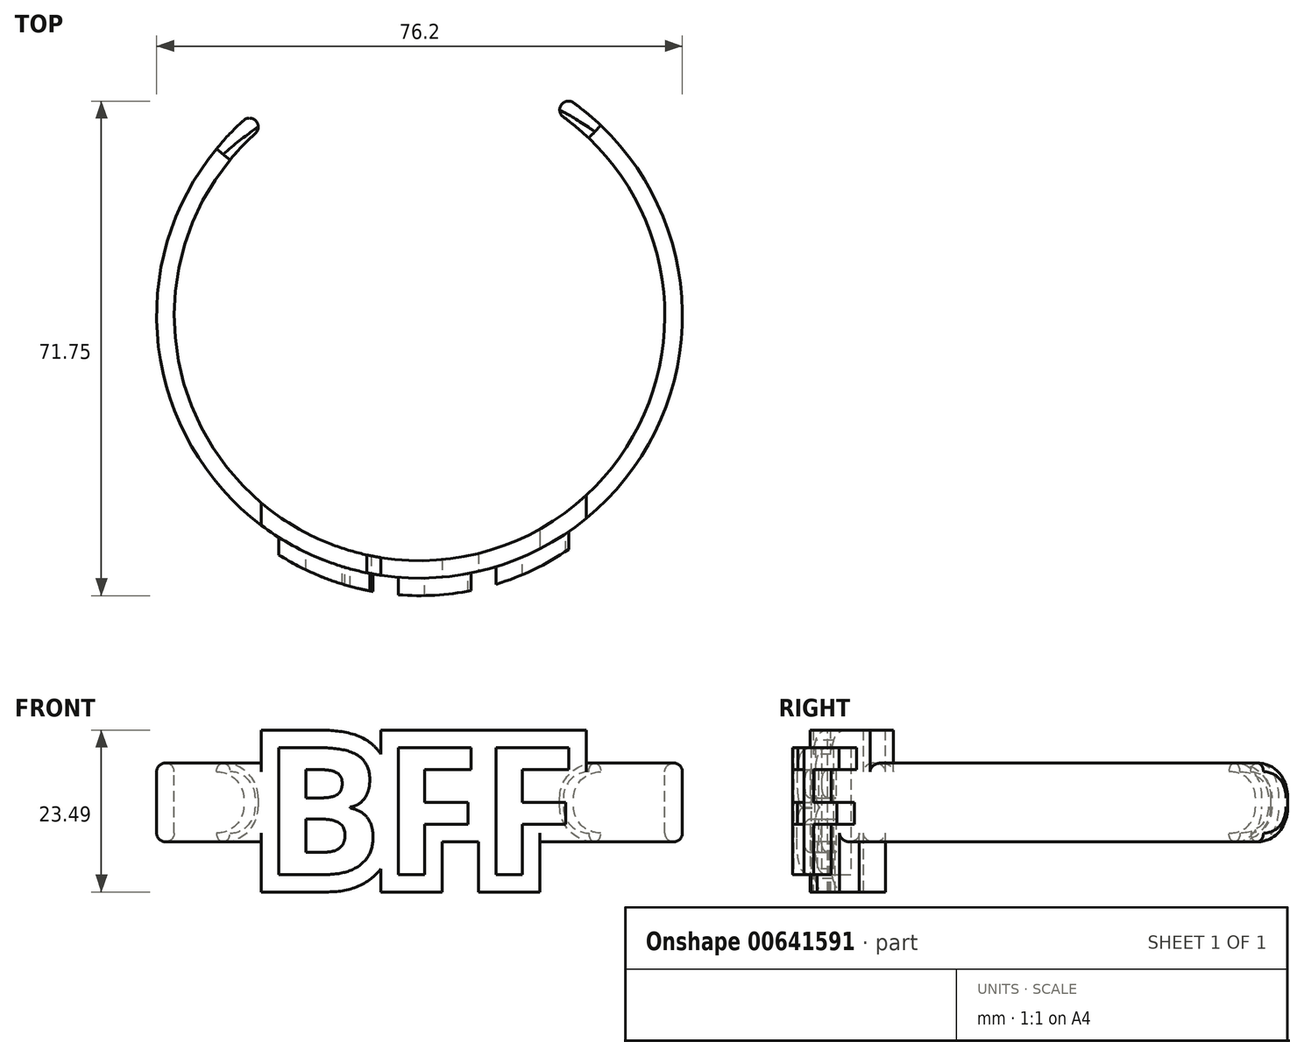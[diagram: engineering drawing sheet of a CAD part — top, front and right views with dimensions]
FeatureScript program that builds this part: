
annotation { "Feature Type Name" : "Feature", "Feature Type Description" : "" }
export const myFeature = defineFeature(function(context is Context, id is Id, definition is map)
    precondition{}
    {
        {
            var Q0;
            Q0=qCreatedBy(makeId("Top.planeOp"),FACE);
            var sketch = newSketch(context, id + "F0", { "sketchPlane" : qUnion([Q0])});
            skCircle(sketch, "E0", {"center": v(0, 0) * mm, "radius": 38.1 * mm});
            skSolve(sketch);
        }
        {
            var Q0;
            Q0 = qSketchRegion(id + "F0", true);
            extrude(context, id + "F1", {"entities" : qUnion([Q0]), "depth" : 25.4 * mm, "offsetDistance" : 25.4 * mm});
        }
        {
            var Q0;
            Q0=qCreatedBy(makeId("Front.planeOp"),FACE);
            var sketch = newSketch(context, id + "F2", { "sketchPlane" : qUnion([Q0])});
            skText(sketch, "E1", { "text": "BFF", "fontName": "OpenSans-Bold.ttf"});
            const initialGuessF2  = {"E1": [-0.0227, 0.00313, 1, 0, 0.01856]};
            skSetInitialGuess(sketch, initialGuessF2);
            skSolve(sketch);
        }
        {
            var Q0;
            Q0 = qSketchRegion(id + "F2", true);
            var Q1;
            Q1=makeQuery(id+"F1.opExtrude","SWEPT_FACE",FACE,{"disambiguationData":[OSD([sQuery(id+"F0.wireOp",EDGE,"E0")])]});
            extrude(context, id + "F3", {"entities" : qUnion([Q0]), "operationType" : NewBodyOperationType.ADD, "endBound" : BoundingType.UP_TO_SURFACE, "depth" : 25.4 * mm, "endBoundEntityFace" : qUnion([Q1]), "hasOffset" : true, "offsetDistance" : 2.54 * mm, "offsetOppositeDirection" : true});
        }
        {
            var Q0;
            Q0=qCreatedBy(makeId("Front.planeOp"),FACE);
            var sketch = newSketch(context, id + "F4", { "sketchPlane" : qUnion([Q0])});
            skLineSegment(sketch, "E2.0", {"start": v(-14.66, 24.08) * mm, "end": v(-22.92, 24.08) * mm});
            skFitSpline(sketch, "E2.1", {"points": [v(-7.62, 22.57) * mm, v(-7.79, 22.68) * mm, v(-8.13, 22.87) * mm, v(-8.63, 23.1) * mm, v(-9.11, 23.3) * mm, v(-9.75, 23.5) * mm, v(-10.52, 23.7) * mm, v(-11.4, 23.86) * mm, v(-12.24, 23.97) * mm, v(-13.34, 24.06) * mm, v(-14.14, 24.08) * mm, v(-14.66, 24.08) * mm]});
            skLineSegment(sketch, "E2.2", {"start": v(-22.92, 24.08) * mm, "end": v(-22.92, 19.3) * mm});
            skFitSpline(sketch, "E2.3", {"points": [v(-4.66, 16.88) * mm, v(-4.66, 17.12) * mm, v(-4.68, 17.61) * mm, v(-4.77, 18.25) * mm, v(-4.88, 18.77) * mm, v(-5.03, 19.3) * mm, v(-5.29, 19.98) * mm, v(-5.65, 20.64) * mm, v(-6, 21.13) * mm, v(-6.3, 21.47) * mm, v(-6.6, 21.8) * mm, v(-7.04, 22.18) * mm, v(-7.39, 22.42) * mm, v(-7.62, 22.57) * mm]});
            skLineSegment(sketch, "E2.5", {"start": v(-22.92, 0.6) * mm, "end": v(-13.5, 0.6) * mm});
            skFitSpline(sketch, "E2.6", {"points": [v(-13.5, 0.6) * mm, v(-13, 0.6) * mm, v(-12.22, 0.63) * mm, v(-11.14, 0.77) * mm, v(-10.3, 0.95) * mm, v(-9.46, 1.2) * mm, v(-8.62, 1.54) * mm, v(-7.8, 1.97) * mm, v(-7.26, 2.33) * mm, v(-7, 2.53) * mm]});
            skFitSpline(sketch, "E2.7", {"points": [v(-7, 2.53) * mm, v(-6.78, 2.7) * mm, v(-6.36, 3.07) * mm, v(-5.77, 3.71) * mm, v(-5.25, 4.44) * mm, v(-4.84, 5.22) * mm, v(-4.53, 6.05) * mm, v(-4.33, 6.87) * mm, v(-4.22, 7.68) * mm, v(-4.2, 8.21) * mm, v(-4.2, 8.47) * mm]});
            skLineSegment(sketch, "E3.0", {"start": v(-5.6, 0.6) * mm, "end": v(3.32, 0.6) * mm});
            skLineSegment(sketch, "E3.1", {"start": v(-5.6, 24.08) * mm, "end": v(-5.6, 20.53) * mm});
            skLineSegment(sketch, "E3.2", {"start": v(3.32, 0.6) * mm, "end": v(3.32, 7.87) * mm});
            skLineSegment(sketch, "E3.4", {"start": v(3.32, 7.87) * mm, "end": v(8.55, 7.87) * mm});
            skLineSegment(sketch, "E4.0", {"start": v(8.55, 0.6) * mm, "end": v(17.47, 0.6) * mm});
            skLineSegment(sketch, "E4.1", {"start": v(8.55, 7.87) * mm, "end": v(8.55, 0.6) * mm});
            skLineSegment(sketch, "E4.2", {"start": v(17.47, 0.6) * mm, "end": v(17.47, 7.87) * mm});
            skLineSegment(sketch, "E4.4", {"start": v(17.47, 7.87) * mm, "end": v(23.7, 7.87) * mm});
            skLineSegment(sketch, "E4.7", {"start": v(24.18, 19.3) * mm, "end": v(24.18, 24.08) * mm});
            skLineSegment(sketch, "E5.trimOffspring", {"start": v(-5.6, 3.95) * mm, "end": v(-5.6, 0.6) * mm});
            skLineSegment(sketch, "E6", {"start": v(-5.6, 24.08) * mm, "end": v(24.18, 24.08) * mm});
            skLineSegment(sketch, "E7.bottom", {"start": v(-48.1, 19.3) * mm, "end": v(-22.92, 19.3) * mm});
            skLineSegment(sketch, "E7.top", {"start": v(-48.1, 7.87) * mm, "end": v(-22.92, 7.87) * mm});
            skLineSegment(sketch, "E8.bottom", {"start": v(24.18, 19.3) * mm, "end": v(51.49, 19.3) * mm});
            skLineSegment(sketch, "E8.top", {"start": v(23.7, 7.87) * mm, "end": v(51.49, 7.87) * mm});
            skLineSegment(sketch, "E8.left", {"start": v(23.7, 7.87) * mm, "end": v(23.7, 7.87) * mm});
            skLineSegment(sketch, "E9.trimOffspring", {"start": v(-22.92, 7.87) * mm, "end": v(-22.92, 0.6) * mm});
            skLineSegment(sketch, "E10", {"start": v(-48.1, 19.3) * mm, "end": v(-48.1, 27.27) * mm});
            skLineSegment(sketch, "E11", {"start": v(-48.1, 27.27) * mm, "end": v(51.82, 27.27) * mm});
            skLineSegment(sketch, "E12", {"start": v(51.82, 27.27) * mm, "end": v(51.49, 19.3) * mm});
            skLineSegment(sketch, "E13", {"start": v(51.49, 7.87) * mm, "end": v(51.49, -5.58) * mm});
            skLineSegment(sketch, "E14", {"start": v(51.49, -5.58) * mm, "end": v(-48.1, -5.58) * mm});
            skLineSegment(sketch, "E15", {"start": v(-48.1, -5.58) * mm, "end": v(-48.1, 7.87) * mm});
            skSolve(sketch);
        }
        {
            var Q0;
            Q0 = qSketchRegion(id + "F4", true);
            extrude(context, id + "F5", {"entities" : qUnion([Q0]), "operationType" : NewBodyOperationType.REMOVE, "endBound" : BoundingType.SYMMETRIC, "oppositeDirection" : true, "depth" : 127 * mm, "offsetDistance" : 25.4 * mm});
        }
        {
            var Q0;
            Q0=qCreatedBy(makeId("Top.planeOp"),FACE);
            var sketch = newSketch(context, id + "F6", { "sketchPlane" : qUnion([Q0])});
            skCircle(sketch, "E16", {"center": v(0, 0) * mm, "radius": 35.56 * mm});
            skSolve(sketch);
        }
        {
            var Q0;
            Q0 = qSketchRegion(id + "F6", true);
            extrude(context, id + "F7", {"entities" : qUnion([Q0]), "operationType" : NewBodyOperationType.REMOVE, "endBound" : BoundingType.SYMMETRIC, "oppositeDirection" : true, "depth" : 127 * mm, "offsetDistance" : 25.4 * mm});
        }
        {
            var Q0;
            Q0=makeQuery(id+"F5.boolean.opBoolean","COPY",FACE,{"derivedFrom":makeQuery(id+"F5.opExtrude","SWEPT_FACE",FACE,{"disambiguationData":[OSD([sQuery(id+"F4.wireOp",EDGE,"E8.bottom")])]})});
            var sketch = newSketch(context, id + "F8", { "sketchPlane" : qUnion([Q0])});
            skLineSegment(sketch, "E17.bottom", {"start": v(-38.63, 46.04) * mm, "end": v(42.06, 46.04) * mm});
            skLineSegment(sketch, "E17.top", {"start": v(-38.63, 18.38) * mm, "end": v(42.06, 18.38) * mm});
            skLineSegment(sketch, "E17.left", {"start": v(-38.63, 46.04) * mm, "end": v(-38.63, 18.38) * mm});
            skLineSegment(sketch, "E17.right", {"start": v(42.06, 46.04) * mm, "end": v(42.06, 18.38) * mm});
            skSolve(sketch);
        }
        {
            var Q0;
            Q0 = qSketchRegion(id + "F8", true);
            extrude(context, id + "F9", {"entities" : qUnion([Q0]), "operationType" : NewBodyOperationType.REMOVE, "depth" : 25.4 * mm, "offsetDistance" : 25.4 * mm});
        }
        {
            var Q0;
            Q0=makeQuery(id+"F5.boolean.opBoolean","COPY",FACE,{"derivedFrom":makeQuery(id+"F5.opExtrude","SWEPT_FACE",FACE,{"disambiguationData":[OSD([sQuery(id+"F4.wireOp",EDGE,"E7.top")])]})});
            var sketch = newSketch(context, id + "F10", { "sketchPlane" : qUnion([Q0])});
            skLineSegment(sketch, "E18.bottom", {"start": v(-23.37, -22.44) * mm, "end": v(20.32, -22.44) * mm});
            skLineSegment(sketch, "E18.top", {"start": v(-23.37, -47.04) * mm, "end": v(20.32, -47.04) * mm});
            skLineSegment(sketch, "E18.left", {"start": v(-23.37, -22.44) * mm, "end": v(-23.37, -47.04) * mm});
            skLineSegment(sketch, "E18.right", {"start": v(20.32, -22.44) * mm, "end": v(20.32, -47.04) * mm});
            skSolve(sketch);
        }
        {
            var Q0;
            Q0 = qSketchRegion(id + "F10", true);
            extrude(context, id + "F11", {"entities" : qUnion([Q0]), "operationType" : NewBodyOperationType.REMOVE, "endBound" : BoundingType.SYMMETRIC, "depth" : 50.8 * mm, "offsetDistance" : 25.4 * mm});
        }
        {
            var Q0;
            Q0=makeQuery(id+"F11.boolean.opBoolean","INTERSECT",EDGE,{"derivedFrom":[makeQuery(id+"F5.boolean.opBoolean","COPY",FACE,{"derivedFrom":makeQuery(id+"F5.opExtrude","SWEPT_FACE",FACE,{"disambiguationData":[OSD([sQuery(id+"F4.wireOp",EDGE,"E7.top")])]})}),makeQuery(id+"F11.opExtrude","SWEPT_FACE",FACE,{"disambiguationData":[OSD([sQuery(id+"F10.wireOp",EDGE,"E18.left")])]})]});
            var Q1;
            Q1=makeQuery(id+"F11.boolean.opBoolean","INTERSECT",EDGE,{"derivedFrom":[makeQuery(id+"F9.boolean.opBoolean","MERGE",FACE,{"derivedFrom":[makeQuery(id+"F5.boolean.opBoolean","COPY",FACE,{"derivedFrom":makeQuery(id+"F5.opExtrude","SWEPT_FACE",FACE,{"disambiguationData":[OSD([sQuery(id+"F4.wireOp",EDGE,"E7.bottom")])]})}),makeQuery(id+"F5.boolean.opBoolean","COPY",FACE,{"derivedFrom":makeQuery(id+"F5.opExtrude","SWEPT_FACE",FACE,{"disambiguationData":[OSD([sQuery(id+"F4.wireOp",EDGE,"E8.bottom")])]})}),makeQuery(id+"F9.opExtrude","CAP_FACE",FACE,{"disambiguationData":[OSD([sQuery(id+"F8.wireOp",EDGE,"E17.bottom"),sQuery(id+"F8.wireOp",EDGE,"E17.top"),sQuery(id+"F8.wireOp",EDGE,"E17.left"),sQuery(id+"F8.wireOp",EDGE,"E17.right")])],"isStart":true})]}),makeQuery(id+"F11.opExtrude","SWEPT_FACE",FACE,{"disambiguationData":[OSD([sQuery(id+"F10.wireOp",EDGE,"E18.left")])]})]});
            var Q2;
            Q2=makeQuery(id+"F11.boolean.opBoolean","INTERSECT",EDGE,{"derivedFrom":[makeQuery(id+"F5.boolean.opBoolean","COPY",FACE,{"derivedFrom":makeQuery(id+"F5.opExtrude","SWEPT_FACE",FACE,{"disambiguationData":[OSD([sQuery(id+"F4.wireOp",EDGE,"E4.4"),sQuery(id+"F4.wireOp",EDGE,"E8.top")])]})}),makeQuery(id+"F11.opExtrude","SWEPT_FACE",FACE,{"disambiguationData":[OSD([sQuery(id+"F10.wireOp",EDGE,"E18.right")])]})]});
            var Q3;
            Q3=makeQuery(id+"F11.boolean.opBoolean","INTERSECT",EDGE,{"derivedFrom":[makeQuery(id+"F9.boolean.opBoolean","MERGE",FACE,{"derivedFrom":[makeQuery(id+"F5.boolean.opBoolean","COPY",FACE,{"derivedFrom":makeQuery(id+"F5.opExtrude","SWEPT_FACE",FACE,{"disambiguationData":[OSD([sQuery(id+"F4.wireOp",EDGE,"E7.bottom")])]})}),makeQuery(id+"F5.boolean.opBoolean","COPY",FACE,{"derivedFrom":makeQuery(id+"F5.opExtrude","SWEPT_FACE",FACE,{"disambiguationData":[OSD([sQuery(id+"F4.wireOp",EDGE,"E8.bottom")])]})}),makeQuery(id+"F9.opExtrude","CAP_FACE",FACE,{"disambiguationData":[OSD([sQuery(id+"F8.wireOp",EDGE,"E17.bottom"),sQuery(id+"F8.wireOp",EDGE,"E17.top"),sQuery(id+"F8.wireOp",EDGE,"E17.left"),sQuery(id+"F8.wireOp",EDGE,"E17.right")])],"isStart":true})]}),makeQuery(id+"F11.opExtrude","SWEPT_FACE",FACE,{"disambiguationData":[OSD([sQuery(id+"F10.wireOp",EDGE,"E18.right")])]})]});
            fillet(context, id + "F12", {"entities" : qUnion([Q0, Q1, Q2, Q3]), "radius" : 5.08 * mm, "tangentPropagation" : true, "allowEdgeOverflow" : false});
        }
        {
            var Q0;
            Q0=makeQuery(id+"F12.opFillet","BLEND_EDGE",EDGE,{"blendedFrom":[makeQuery(id+"F11.boolean.opBoolean","INTERSECT",EDGE,{"derivedFrom":[makeQuery(id+"F9.boolean.opBoolean","MERGE",FACE,{"derivedFrom":[makeQuery(id+"F5.boolean.opBoolean","COPY",FACE,{"derivedFrom":makeQuery(id+"F5.opExtrude","SWEPT_FACE",FACE,{"disambiguationData":[OSD([sQuery(id+"F4.wireOp",EDGE,"E7.bottom")])]})}),makeQuery(id+"F5.boolean.opBoolean","COPY",FACE,{"derivedFrom":makeQuery(id+"F5.opExtrude","SWEPT_FACE",FACE,{"disambiguationData":[OSD([sQuery(id+"F4.wireOp",EDGE,"E8.bottom")])]})}),makeQuery(id+"F9.opExtrude","CAP_FACE",FACE,{"disambiguationData":[OSD([sQuery(id+"F8.wireOp",EDGE,"E17.bottom"),sQuery(id+"F8.wireOp",EDGE,"E17.top"),sQuery(id+"F8.wireOp",EDGE,"E17.left"),sQuery(id+"F8.wireOp",EDGE,"E17.right")])],"isStart":true})]}),makeQuery(id+"F11.opExtrude","SWEPT_FACE",FACE,{"disambiguationData":[OSD([sQuery(id+"F10.wireOp",EDGE,"E18.right")])]})]}),makeQuery(id+"F7.boolean.opBoolean","COPY",FACE,{"derivedFrom":makeQuery(id+"F7.opExtrude","SWEPT_FACE",FACE,{"disambiguationData":[OSD([sQuery(id+"F6.wireOp",EDGE,"E16")])]})})],"blendedInto":[makeQuery(id+"F7.boolean.opBoolean","COPY",FACE,{"derivedFrom":makeQuery(id+"F7.opExtrude","SWEPT_FACE",FACE,{"disambiguationData":[OSD([sQuery(id+"F6.wireOp",EDGE,"E16")])]})})]});
            var Q1;
            {var subQ0=sQuery(id+"F0.wireOp",EDGE,"E0");Q1=makeQuery(id+"F12.opFillet","BLEND_EDGE",EDGE,{"blendedFrom":[makeQuery(id+"F11.boolean.opBoolean","INTERSECT",EDGE,{"derivedFrom":[makeQuery(id+"F9.boolean.opBoolean","MERGE",FACE,{"derivedFrom":[makeQuery(id+"F5.boolean.opBoolean","COPY",FACE,{"derivedFrom":makeQuery(id+"F5.opExtrude","SWEPT_FACE",FACE,{"disambiguationData":[OSD([sQuery(id+"F4.wireOp",EDGE,"E7.bottom")])]})}),makeQuery(id+"F5.boolean.opBoolean","COPY",FACE,{"derivedFrom":makeQuery(id+"F5.opExtrude","SWEPT_FACE",FACE,{"disambiguationData":[OSD([sQuery(id+"F4.wireOp",EDGE,"E8.bottom")])]})})],"fromTools":[makeQuery(id+"F9.opExtrude","CAP_FACE",FACE,{"disambiguationData":[OSD([sQuery(id+"F8.wireOp",EDGE,"E17.bottom"),sQuery(id+"F8.wireOp",EDGE,"E17.top"),sQuery(id+"F8.wireOp",EDGE,"E17.left"),sQuery(id+"F8.wireOp",EDGE,"E17.right")])],"isStart":true})]}),makeQuery(id+"F11.opExtrude","SWEPT_FACE",FACE,{"disambiguationData":[OSD([sQuery(id+"F10.wireOp",EDGE,"E18.right")])]})]}),makeQuery(id+"F3.boolean.opBoolean","SPLIT",FACE,{"disambiguationData":[TD([makeQuery(id+"F1.opExtrude","CAP_FACE",FACE,{"disambiguationData":[OSD([subQ0])],"isStart":true})])],"derivedFrom":makeQuery(id+"F1.opExtrude","SWEPT_FACE",FACE,{"disambiguationData":[OSD([subQ0])]})})],"blendedInto":[makeQuery(id+"F3.boolean.opBoolean","SPLIT",FACE,{"disambiguationData":[TD([makeQuery(id+"F1.opExtrude","CAP_FACE",FACE,{"disambiguationData":[OSD([subQ0])],"isStart":true})])],"derivedFrom":makeQuery(id+"F1.opExtrude","SWEPT_FACE",FACE,{"disambiguationData":[OSD([subQ0])]})})]});}
            var Q2;
            {var subQ0=makeQuery(id+"F5.opExtrude","SWEPT_FACE",FACE,{"disambiguationData":[OSD([sQuery(id+"F4.wireOp",EDGE,"E8.bottom")])]});var subQ1=makeQuery(id+"F5.opExtrude","SWEPT_FACE",FACE,{"disambiguationData":[OSD([sQuery(id+"F4.wireOp",EDGE,"E7.bottom")])]});var subQ2=sQuery(id+"F0.wireOp",EDGE,"E0");var subQ3=makeQuery(id+"F1.opExtrude","SWEPT_FACE",FACE,{"disambiguationData":[OSD([subQ2])]});var subQ4=makeQuery(id+"F3.boolean.opBoolean","SPLIT",FACE,{"disambiguationData":[TD([makeQuery(id+"F1.opExtrude","CAP_FACE",FACE,{"disambiguationData":[OSD([subQ2])],"isStart":true})])],"derivedFrom":subQ3});Q2=makeQuery(id+"F11.boolean.opBoolean","SPLIT",EDGE,{"disambiguationData":[TD([makeQuery(id+"F5.boolean.opBoolean","COPY",FACE,{"derivedFrom":makeQuery(id+"F5.opExtrude","SWEPT_FACE",FACE,{"disambiguationData":[OSD([sQuery(id+"F4.wireOp",EDGE,"E2.2")])]})})])],"derivedFrom":makeQuery(id+"F9.boolean.opBoolean","MERGE",EDGE,{"derivedFrom":[makeQuery(id+"F5.boolean.opBoolean","INTERSECT",EDGE,{"derivedFrom":[subQ4,subQ1]}),makeQuery(id+"F5.boolean.opBoolean","INTERSECT",EDGE,{"derivedFrom":[subQ4,subQ0]})]})});}
            var Q3;
            {var subQ0=makeQuery(id+"F7.opExtrude","SWEPT_FACE",FACE,{"disambiguationData":[OSD([sQuery(id+"F6.wireOp",EDGE,"E16")])]});var subQ1=makeQuery(id+"F5.boolean.opBoolean","COPY",FACE,{"derivedFrom":makeQuery(id+"F5.opExtrude","SWEPT_FACE",FACE,{"disambiguationData":[OSD([sQuery(id+"F4.wireOp",EDGE,"E8.bottom")])]})});var subQ2=makeQuery(id+"F5.boolean.opBoolean","COPY",FACE,{"derivedFrom":makeQuery(id+"F5.opExtrude","SWEPT_FACE",FACE,{"disambiguationData":[OSD([sQuery(id+"F4.wireOp",EDGE,"E7.bottom")])]})});Q3=makeQuery(id+"F11.boolean.opBoolean","SPLIT",EDGE,{"disambiguationData":[TD([makeQuery(id+"F5.boolean.opBoolean","COPY",FACE,{"derivedFrom":makeQuery(id+"F5.opExtrude","SWEPT_FACE",FACE,{"disambiguationData":[OSD([sQuery(id+"F4.wireOp",EDGE,"E2.2")])]})})])],"derivedFrom":makeQuery(id+"F9.boolean.opBoolean","MERGE",EDGE,{"derivedFrom":[makeQuery(id+"F7.boolean.opBoolean","INTERSECT",EDGE,{"derivedFrom":[subQ2,subQ0]}),makeQuery(id+"F7.boolean.opBoolean","INTERSECT",EDGE,{"derivedFrom":[subQ1,subQ0]})]})});}
            fillet(context, id + "F13", {"entities" : qUnion([Q0, Q1, Q2, Q3]), "radius" : 1.27 * mm, "tangentPropagation" : true, "allowEdgeOverflow" : false});
        }
    });
